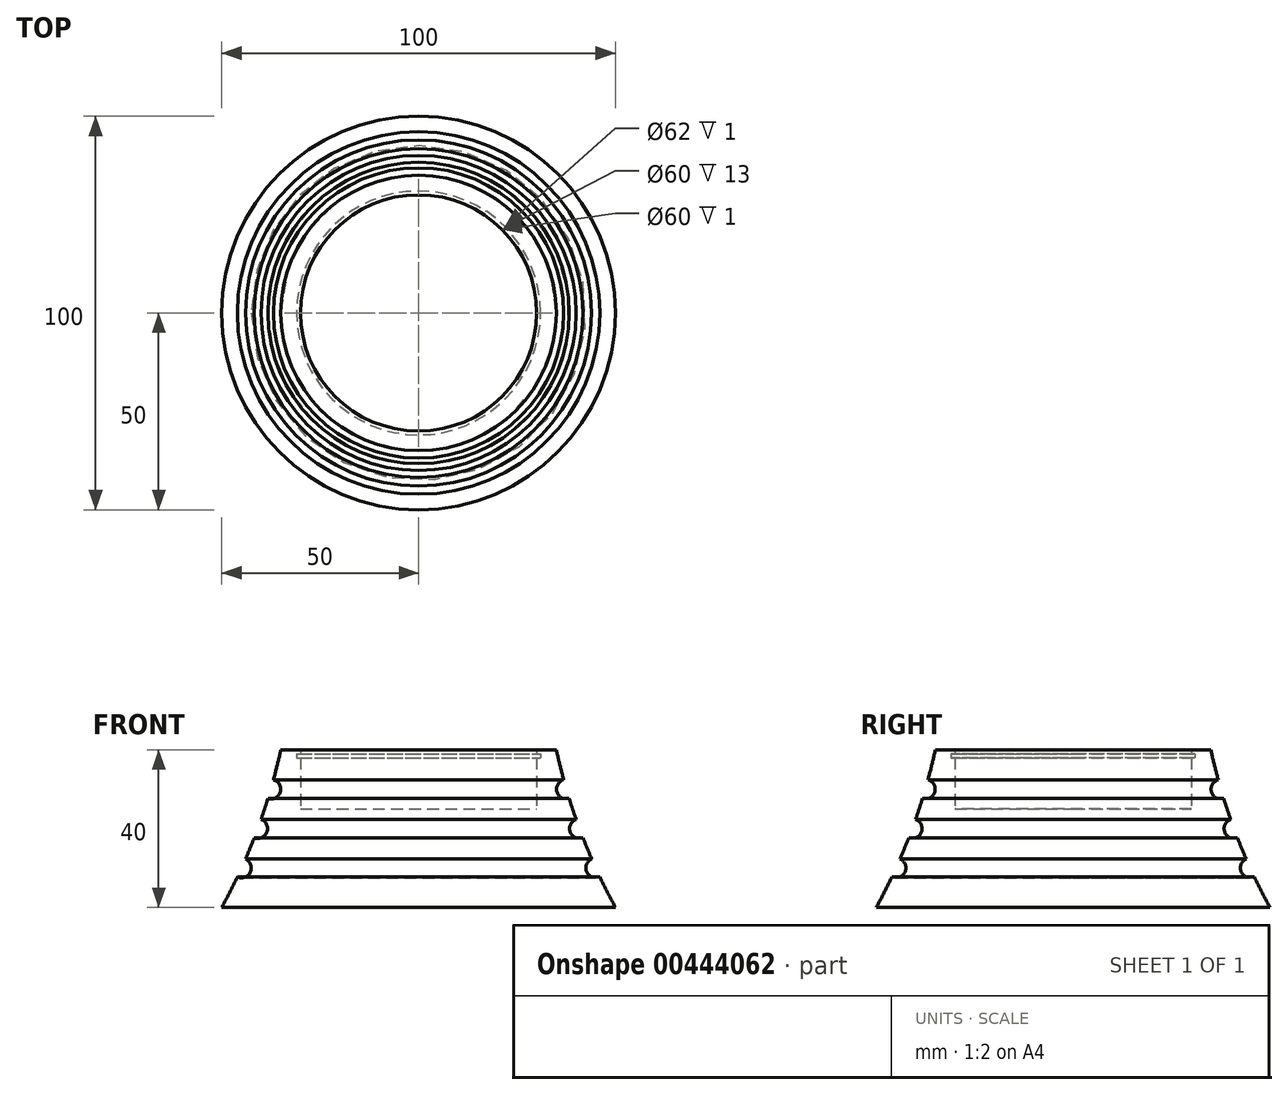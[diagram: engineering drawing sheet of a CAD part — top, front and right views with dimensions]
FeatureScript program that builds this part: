
annotation { "Feature Type Name" : "Feature", "Feature Type Description" : "" }
export const myFeature = defineFeature(function(context is Context, id is Id, definition is map)
    precondition{}
    {
        {
            var Q0;
            Q0=qCreatedBy(makeId("Front.planeOp"),FACE);
            var sketch = newSketch(context, id + "F0", { "sketchPlane" : qUnion([Q0])});
            skLineSegment(sketch, "E0", {"start": v(0, 0) * mm, "end": v(0, 25) * mm});
            skLineSegment(sketch, "E1", {"start": v(30, 25) * mm, "end": v(0, 25) * mm});
            skLineSegment(sketch, "E2", {"start": v(30, 25) * mm, "end": v(30, 38) * mm});
            skLineSegment(sketch, "E3", {"start": v(30, 40) * mm, "end": v(35, 40) * mm});
            skLineSegment(sketch, "E4", {"start": v(0, 0) * mm, "end": v(50, 0) * mm});
            skArc(sketch, "E5", {"start": v(35, 40) * mm, "mid": v(35.89, 36.2) * mm, "end": v(36.87, 32.4) * mm});
            skLineSegment(sketch, "E6.bottom", {"start": v(30, 39) * mm, "end": v(31, 39) * mm});
            skLineSegment(sketch, "E6.top", {"start": v(30, 38) * mm, "end": v(31, 38) * mm});
            skLineSegment(sketch, "E6.right", {"start": v(31, 39) * mm, "end": v(31, 38) * mm});
            skLineSegment(sketch, "E7.trimOffspring", {"start": v(30, 39) * mm, "end": v(30, 40) * mm});
            skArc(sketch, "E8", {"start": v(36.87, 32.4) * mm, "mid": v(35.16, 29.3) * mm, "end": v(38.28, 27.6) * mm});
            skArc(sketch, "E9", {"start": v(43.97, 12.28) * mm, "mid": v(42.72, 8.96) * mm, "end": v(46.05, 7.73) * mm});
            skArc(sketch, "E10", {"start": v(40.02, 22.35) * mm, "mid": v(38.52, 19.13) * mm, "end": v(41.76, 17.66) * mm});
            skArc(sketch, "E11.trimOffspring", {"start": v(41.76, 17.66) * mm, "mid": v(42.84, 14.96) * mm, "end": v(43.97, 12.28) * mm});
            skArc(sketch, "E12.trimOffspring", {"start": v(38.28, 27.6) * mm, "mid": v(39.12, 24.97) * mm, "end": v(40.02, 22.35) * mm});
            skArc(sketch, "E13.trimOffspring", {"start": v(46.05, 7.73) * mm, "mid": v(47.97, 3.84) * mm, "end": v(50, 0) * mm});
            skSolve(sketch);
        }
        {
            var Q0;
            Q0 = qSketchRegion(id + "F0", true);
            var Q1;
            Q1=sQuery(id+"F0.wireOp",EDGE,"E0");
            revolve(context, id + "F1", {"entities" : qUnion([Q0]), "axis" : qUnion([Q1]), "revolveType" : RevolveType.FULL});
        }
    });
